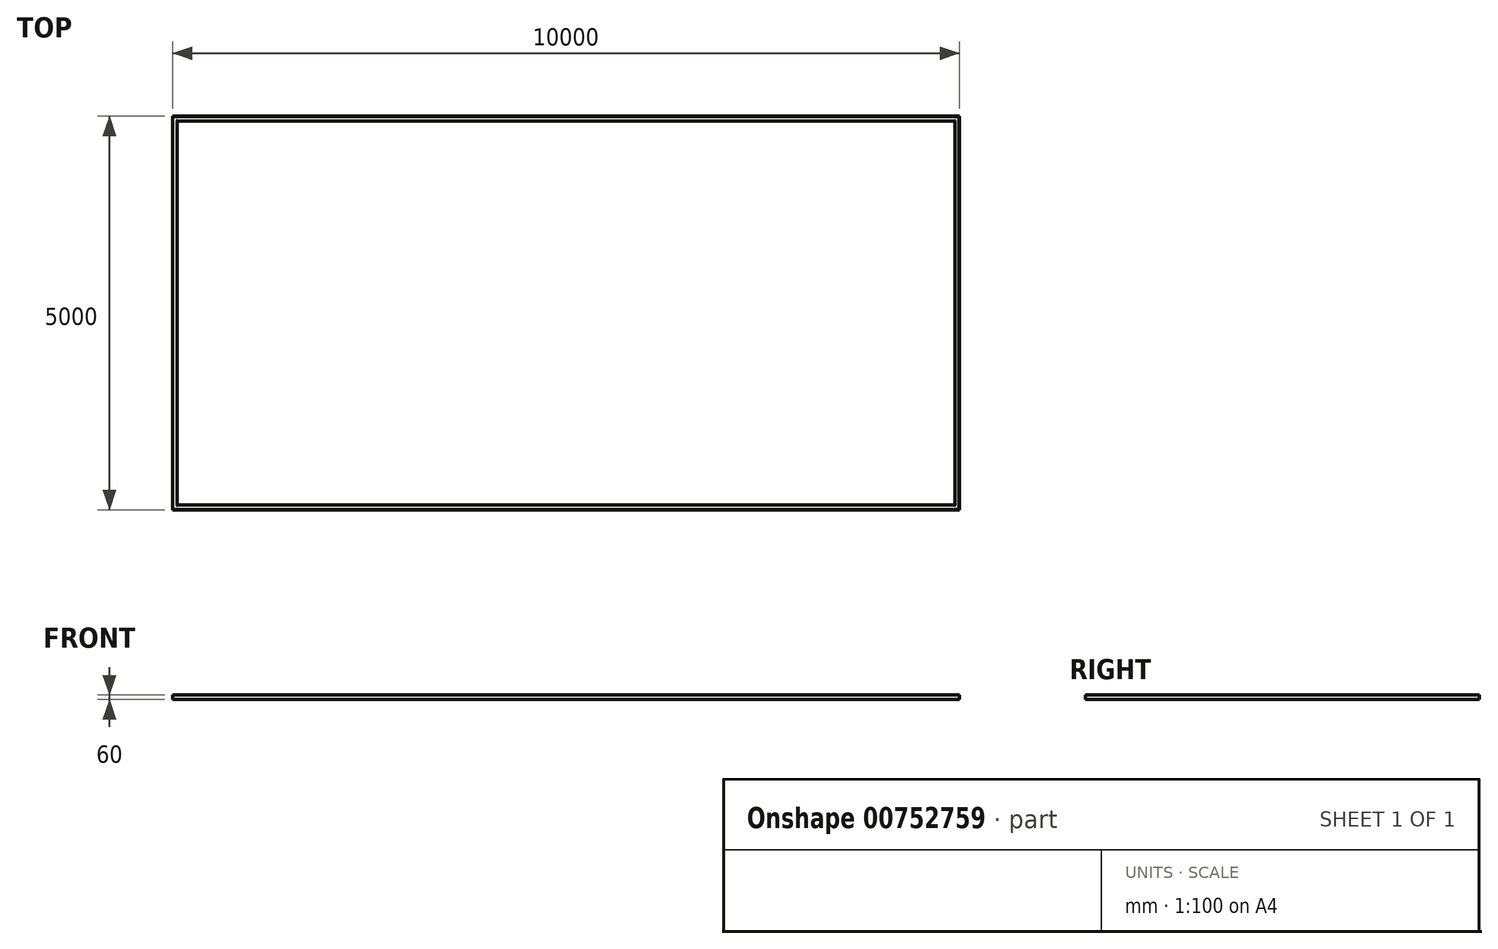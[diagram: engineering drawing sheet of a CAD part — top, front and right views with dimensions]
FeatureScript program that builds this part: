
annotation { "Feature Type Name" : "Feature", "Feature Type Description" : "" }
export const myFeature = defineFeature(function(context is Context, id is Id, definition is map)
    precondition{}
    {
        {
            var Q0;
            Q0=qCreatedBy(makeId("Top.planeOp"),FACE);
            var sketch = newSketch(context, id + "F0", { "sketchPlane" : qUnion([Q0])});
            skLineSegment(sketch, "E0.bottom", {"start": v(5000, 2500) * mm, "end": v(-5000, 2500) * mm});
            skLineSegment(sketch, "E0.top", {"start": v(5000, -2500) * mm, "end": v(-5000, -2500) * mm});
            skLineSegment(sketch, "E0.left", {"start": v(5000, 2500) * mm, "end": v(5000, -2500) * mm});
            skLineSegment(sketch, "E0.right", {"start": v(-5000, 2500) * mm, "end": v(-5000, -2500) * mm});
            skPoint(sketch, "E0.middle", {"position": v(0, 0) * mm});
            skSolve(sketch);
        }
        {
            var Q0;
            Q0=qCreatedBy(makeId("Right.planeOp"),FACE);
            var sketch = newSketch(context, id + "F1", { "sketchPlane" : qUnion([Q0])});
            skLineSegment(sketch, "E1", {"start": v(2500, 0) * mm, "end": v(2500, 60) * mm});
            skLineSegment(sketch, "E2", {"start": v(2500, 60) * mm, "end": v(2499, 60) * mm});
            skLineSegment(sketch, "E3", {"start": v(2494, 55) * mm, "end": v(2494, 11) * mm});
            skLineSegment(sketch, "E4", {"start": v(2489, 6) * mm, "end": v(2445, 6) * mm});
            skLineSegment(sketch, "E5", {"start": v(2440, 1) * mm, "end": v(2440, 0) * mm});
            skLineSegment(sketch, "E6", {"start": v(2440, 0) * mm, "end": v(2500, 0) * mm});
            skPoint(sketch, "E7.visualSharp", {"position": v(2494, 60) * mm});
            skArc(sketch, "E7.filletArc", {"start": v(2499, 60) * mm, "mid": v(2495.46, 58.54) * mm, "end": v(2494, 55) * mm});
            skPoint(sketch, "E8.visualSharp", {"position": v(2440, 6) * mm});
            skArc(sketch, "E8.filletArc", {"start": v(2445, 6) * mm, "mid": v(2441.46, 4.54) * mm, "end": v(2440, 1) * mm});
            skPoint(sketch, "E9.visualSharp", {"position": v(2494, 6) * mm});
            skArc(sketch, "E9.filletArc", {"start": v(2489, 6) * mm, "mid": v(2492.54, 7.46) * mm, "end": v(2494, 11) * mm});
            skSolve(sketch);
        }
        {
            var Q0;
            Q0 = qSketchRegion(id + "F1", true);
            var Q1;
            Q1 = qConstructionFilter(qBodyType(qCreatedBy(id + "F0" ,EDGE), BodyType.WIRE), ConstructionObject.NO);
            sweep(context, id + "F2", {"profiles" : qUnion([Q0]), "path" : qUnion([Q1])});
        }
    });
